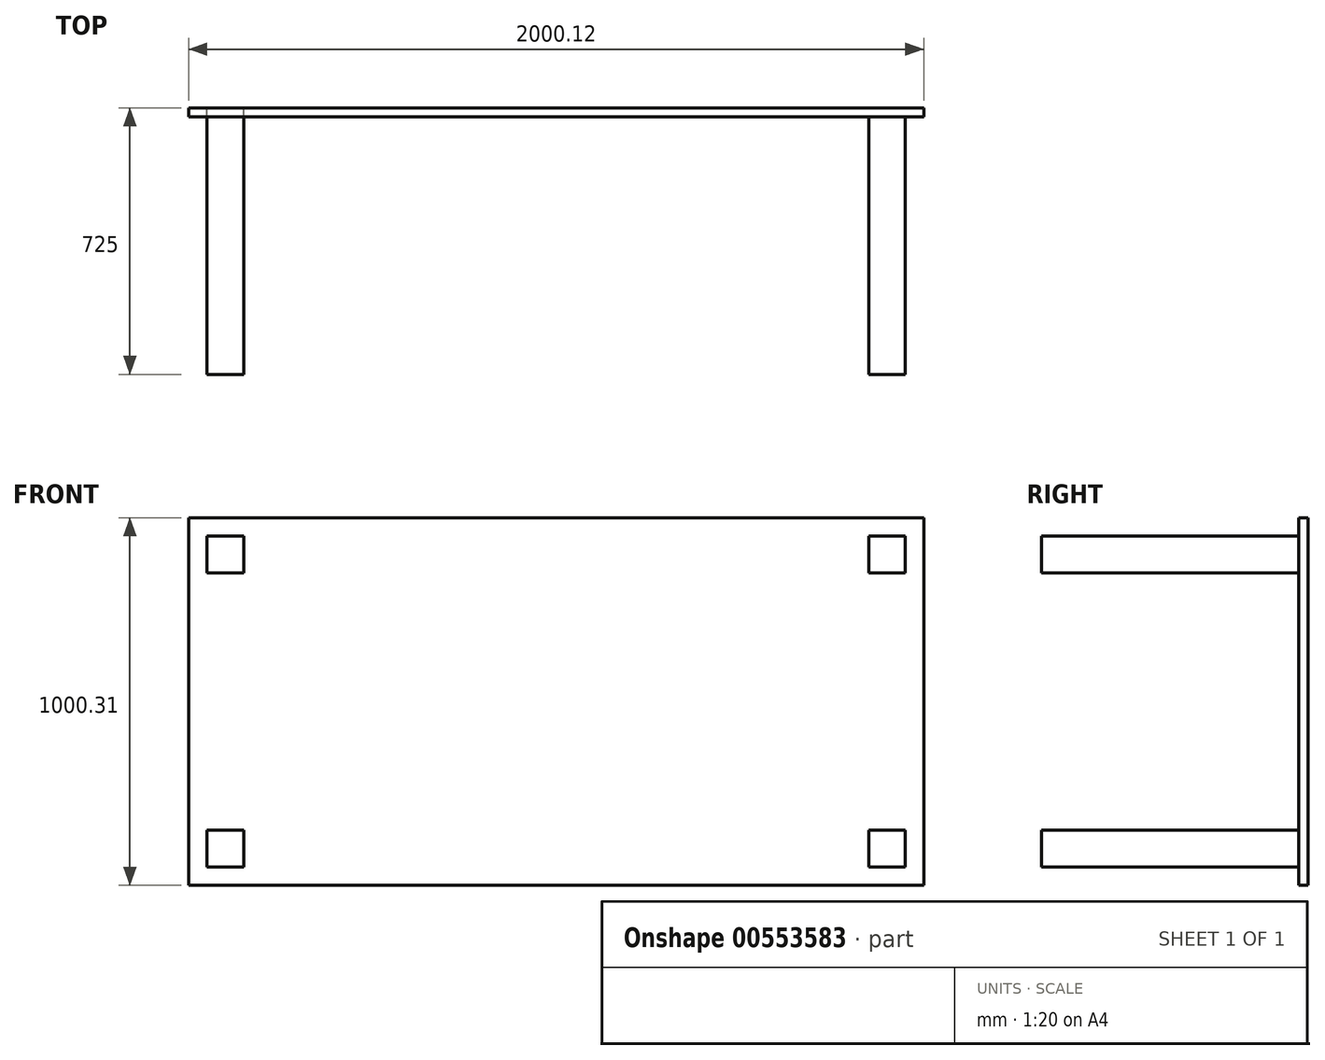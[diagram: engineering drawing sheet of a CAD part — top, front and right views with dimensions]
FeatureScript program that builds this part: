
annotation { "Feature Type Name" : "Feature", "Feature Type Description" : "" }
export const myFeature = defineFeature(function(context is Context, id is Id, definition is map)
    precondition{}
    {
        {
            var Q0;
            Q0=qCreatedBy(makeId("Front.planeOp"),FACE);
            var sketch = newSketch(context, id + "F0", { "sketchPlane" : qUnion([Q0])});
            skLineSegment(sketch, "E0.bottom", {"start": v(1237.7, 726.26) * mm, "end": v(-762.41, 726.26) * mm});
            skLineSegment(sketch, "E0.top", {"start": v(1237.7, -274.05) * mm, "end": v(-762.41, -274.05) * mm});
            skLineSegment(sketch, "E0.left", {"start": v(1237.7, 726.26) * mm, "end": v(1237.7, -274.05) * mm});
            skLineSegment(sketch, "E0.right", {"start": v(-762.41, 726.26) * mm, "end": v(-762.41, -274.05) * mm});
            skSolve(sketch);
        }
        {
            var Q0;
            Q0=makeQuery(id+"F0.imprint","IMPRINT",FACE,{"disambiguationData":[TD([[makeQuery(id+"F0.imprint","IMPRINT",EDGE,{"derivedFrom":sQuery(id+"F0.wireOp",EDGE,"E0.bottom")}),1.0]])]});
            extrude(context, id + "F1", {"entities" : qUnion([Q0]), "depth" : 25 * mm, "offsetDistance" : 25 * mm});
        }
        {
            var Q0;
            Q0=qCreatedBy(makeId("Front.planeOp"),FACE);
            var sketch = newSketch(context, id + "F2", { "sketchPlane" : qUnion([Q0])});
            skLineSegment(sketch, "E1.bottom", {"start": v(-712.41, -224.05) * mm, "end": v(-612.41, -224.05) * mm});
            skLineSegment(sketch, "E1.top", {"start": v(-712.41, -124.05) * mm, "end": v(-612.41, -124.05) * mm});
            skLineSegment(sketch, "E1.left", {"start": v(-712.41, -224.05) * mm, "end": v(-712.41, -124.05) * mm});
            skLineSegment(sketch, "E1.right", {"start": v(-612.41, -224.05) * mm, "end": v(-612.41, -124.05) * mm});
            skSolve(sketch);
        }
        {
            var Q0;
            Q0=makeQuery(id+"F2.imprint","IMPRINT",FACE,{"disambiguationData":[TD([[makeQuery(id+"F2.imprint","IMPRINT",EDGE,{"derivedFrom":sQuery(id+"F2.wireOp",EDGE,"E1.bottom")}),1.0]])]});
            extrude(context, id + "F3", {"entities" : qUnion([Q0]), "operationType" : NewBodyOperationType.ADD, "depth" : 725 * mm, "offsetDistance" : 25 * mm});
        }
        {
            var Q0;
            Q0=qCreatedBy(makeId("Front.planeOp"),FACE);
            var sketch = newSketch(context, id + "F4", { "sketchPlane" : qUnion([Q0])});
            skLineSegment(sketch, "E2.bottom", {"start": v(1187.7, 676.26) * mm, "end": v(1087.7, 676.26) * mm});
            skLineSegment(sketch, "E2.top", {"start": v(1187.7, 576.26) * mm, "end": v(1087.7, 576.26) * mm});
            skLineSegment(sketch, "E2.left", {"start": v(1187.7, 676.26) * mm, "end": v(1187.7, 576.26) * mm});
            skLineSegment(sketch, "E2.right", {"start": v(1087.7, 676.26) * mm, "end": v(1087.7, 576.26) * mm});
            skSolve(sketch);
        }
        {
            var Q0;
            Q0 = qSketchRegion(id + "F4", true);
            extrude(context, id + "F5", {"entities" : qUnion([Q0]), "operationType" : NewBodyOperationType.ADD, "depth" : 725 * mm, "offsetDistance" : 25 * mm});
        }
        {
            var Q0;
            Q0=qCreatedBy(makeId("Front.planeOp"),FACE);
            var sketch = newSketch(context, id + "F6", { "sketchPlane" : qUnion([Q0])});
            skLineSegment(sketch, "E3.bottom", {"start": v(-612.41, 676.26) * mm, "end": v(-712.41, 676.26) * mm});
            skLineSegment(sketch, "E3.top", {"start": v(-612.41, 576.26) * mm, "end": v(-712.41, 576.26) * mm});
            skLineSegment(sketch, "E3.left", {"start": v(-612.41, 676.26) * mm, "end": v(-612.41, 576.26) * mm});
            skLineSegment(sketch, "E3.right", {"start": v(-712.41, 676.26) * mm, "end": v(-712.41, 576.26) * mm});
            skSolve(sketch);
        }
        {
            var Q0;
            Q0=makeQuery(id+"F6.imprint","IMPRINT",FACE,{"disambiguationData":[TD([[makeQuery(id+"F6.imprint","IMPRINT",EDGE,{"derivedFrom":sQuery(id+"F6.wireOp",EDGE,"E3.bottom")}),1.0]])]});
            extrude(context, id + "F7", {"entities" : qUnion([Q0]), "depth" : 725 * mm, "offsetDistance" : 25 * mm});
        }
        {
            var Q0;
            Q0=qCreatedBy(makeId("Front.planeOp"),FACE);
            var sketch = newSketch(context, id + "F8", { "sketchPlane" : qUnion([Q0])});
            skLineSegment(sketch, "E4.bottom", {"start": v(1187.7, -124.05) * mm, "end": v(1087.7, -124.05) * mm});
            skLineSegment(sketch, "E4.top", {"start": v(1187.7, -224.05) * mm, "end": v(1087.7, -224.05) * mm});
            skLineSegment(sketch, "E4.left", {"start": v(1187.7, -124.05) * mm, "end": v(1187.7, -224.05) * mm});
            skLineSegment(sketch, "E4.right", {"start": v(1087.7, -124.05) * mm, "end": v(1087.7, -224.05) * mm});
            skSolve(sketch);
        }
        {
            var Q0;
            Q0 = qSketchRegion(id + "F8", true);
            extrude(context, id + "F9", {"entities" : qUnion([Q0]), "operationType" : NewBodyOperationType.ADD, "depth" : 725 * mm, "offsetDistance" : 25 * mm});
        }
    });
